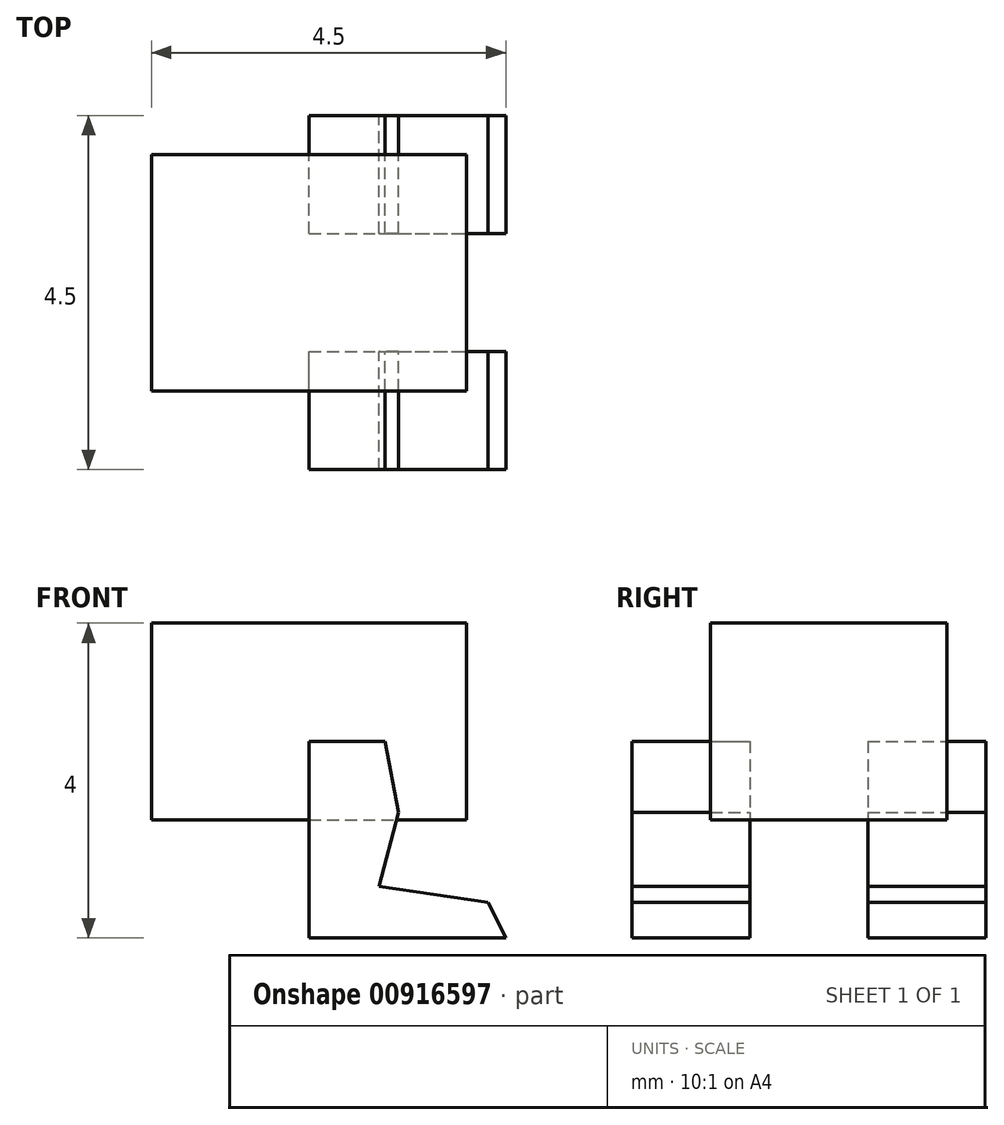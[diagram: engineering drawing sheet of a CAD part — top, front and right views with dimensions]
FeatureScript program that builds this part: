
annotation { "Feature Type Name" : "Feature", "Feature Type Description" : "" }
export const myFeature = defineFeature(function(context is Context, id is Id, definition is map)
    precondition{}
    {
        {
            var Q0;
            Q0=qCreatedBy(makeId("Front.planeOp"),FACE);
            var sketch = newSketch(context, id + "F0", { "sketchPlane" : qUnion([Q0])});
            skLineSegment(sketch, "E0.bottom", {"start": v(0, 0) * mm, "end": v(4, 0) * mm});
            skLineSegment(sketch, "E0.top", {"start": v(0, 2.5) * mm, "end": v(4, 2.5) * mm});
            skLineSegment(sketch, "E0.left", {"start": v(0, 0) * mm, "end": v(0, 2.5) * mm});
            skLineSegment(sketch, "E0.right", {"start": v(4, 0) * mm, "end": v(4, 2.5) * mm});
            skSolve(sketch);
        }
        {
            var Q0;
            Q0=makeQuery(id+"F0.imprint","IMPRINT",FACE,{"disambiguationData":[TD([[makeQuery(id+"F0.imprint","IMPRINT",EDGE,{"derivedFrom":sQuery(id+"F0.wireOp",EDGE,"E0.bottom")}),1.0]])]});
            extrude(context, id + "F1", {"entities" : qUnion([Q0]), "depth" : 3 * mm, "offsetDistance" : 25 * mm});
        }
        {
            var Q0;
            Q0=qCreatedBy(makeId("Front.planeOp"),FACE);
            var sketch = newSketch(context, id + "F2", { "sketchPlane" : qUnion([Q0])});
            skLineSegment(sketch, "E1.bottom", {"start": v(4.9, 1) * mm, "end": v(5.86, 1) * mm});
            skLineSegment(sketch, "E1.top", {"start": v(4.9, -1.5) * mm, "end": v(7.4, -1.5) * mm});
            skLineSegment(sketch, "E1.left", {"start": v(4.9, 1) * mm, "end": v(4.9, -1.5) * mm});
            skLineSegment(sketch, "E2", {"start": v(5.86, 1) * mm, "end": v(6.03, 0.09) * mm});
            skLineSegment(sketch, "E3", {"start": v(6.03, 0.09) * mm, "end": v(5.79, -0.85) * mm});
            skLineSegment(sketch, "E4", {"start": v(5.79, -0.85) * mm, "end": v(7.17, -1.05) * mm});
            skLineSegment(sketch, "E5", {"start": v(7.17, -1.05) * mm, "end": v(7.4, -1.5) * mm});
            skSolve(sketch);
        }
        {
            var Q0;
            Q0=makeQuery(id+"F2.imprint","IMPRINT",FACE,{"disambiguationData":[TD([[makeQuery(id+"F2.imprint","IMPRINT",EDGE,{"derivedFrom":sQuery(id+"F2.wireOp",EDGE,"E1.bottom")}),-1.0]])]});
            extrude(context, id + "F3", {"entities" : qUnion([Q0]), "depth" : 1.5 * mm, "offsetDistance" : 25 * mm});
        }
        {
            var Q0;
            Q0=makeQuery(id+"F1.opExtrude","CAP_EDGE",EDGE,{"disambiguationData":[OSD([sQuery(id+"F0.wireOp",EDGE,"E0.bottom")])],"isStart":false});
            cPoint(context, id + "F4", {"entities" : qUnion([Q0]), "parameter" : 0.5});
        }
        {
            var Q0;
            Q0=makeQuery(id+"F3.opExtrude","SWEPT_BODY",BODY,{"disambiguationData":[OSD([sQuery(id+"F2.wireOp",EDGE,"E1.bottom"),sQuery(id+"F2.wireOp",EDGE,"E1.top"),sQuery(id+"F2.wireOp",EDGE,"E1.left"),sQuery(id+"F2.wireOp",EDGE,"E2"),sQuery(id+"F2.wireOp",EDGE,"E3"),sQuery(id+"F2.wireOp",EDGE,"E4"),sQuery(id+"F2.wireOp",EDGE,"E5")])]});
            var Q1;
            Q1=makeQuery(id+"F3.opExtrude","CAP_VERTEX",VERTEX,{"disambiguationData":[OSD([sQuery(id+"F2.wireOp",EDGE,"E1.bottom"),sQuery(id+"F2.wireOp",EDGE,"E1.left")])],"isStart":true});
            var Q2;
            Q2 = qCreatedBy(id + "F4" ,VERTEX);
            transform(context, id + "F5", {"entities" : qUnion([Q0]), "transformType" : TransformType.TRANSLATION_ENTITY, "oppositeDirectionEntity" : false, "transformLine" : qUnion([Q1, Q2]), "makeCopy" : false});
        }
        {
            var Q0;
            Q0=makeQuery(id+"F1.opExtrude","CAP_EDGE",EDGE,{"disambiguationData":[OSD([sQuery(id+"F0.wireOp",EDGE,"E0.bottom")])],"isStart":false});
            cPoint(context, id + "F6", {"entities" : qUnion([Q0]), "parameter" : 0.5});
        }
        {
            var Q0;
            Q0=makeQuery(id+"F3.opExtrude","SWEPT_BODY",BODY,{"disambiguationData":[OSD([sQuery(id+"F2.wireOp",EDGE,"E1.bottom"),sQuery(id+"F2.wireOp",EDGE,"E1.top"),sQuery(id+"F2.wireOp",EDGE,"E1.left"),sQuery(id+"F2.wireOp",EDGE,"E2"),sQuery(id+"F2.wireOp",EDGE,"E3"),sQuery(id+"F2.wireOp",EDGE,"E4"),sQuery(id+"F2.wireOp",EDGE,"E5")])]});
            var Q1;
            Q1 = qCreatedBy(id + "F6" ,VERTEX);
            var Q2;
            Q2=makeQuery(id+"F1.opExtrude","SWEPT_FACE",FACE,{"disambiguationData":[OSD([sQuery(id+"F0.wireOp",EDGE,"E0.top")])]});
            transform(context, id + "F7", {"entities" : qUnion([Q0]), "transformType" : TransformType.TRANSLATION_DISTANCE, "transformDirection" : qUnion([Q2]), "distance" : 1 * mm, "makeCopy" : false});
        }
        {
            var Q0;
            Q0=makeQuery(id+"F3.opExtrude","SWEPT_BODY",BODY,{"disambiguationData":[OSD([sQuery(id+"F2.wireOp",EDGE,"E1.bottom"),sQuery(id+"F2.wireOp",EDGE,"E1.top"),sQuery(id+"F2.wireOp",EDGE,"E1.left"),sQuery(id+"F2.wireOp",EDGE,"E2"),sQuery(id+"F2.wireOp",EDGE,"E3"),sQuery(id+"F2.wireOp",EDGE,"E4"),sQuery(id+"F2.wireOp",EDGE,"E5")])]});
            var Q1;
            Q1=qCreatedBy(makeId("Right.planeOp"),FACE);
            var Q2;
            Q2=qCreatedBy(makeId("Front.planeOp"),FACE);
            transform(context, id + "F8", {"entities" : qUnion([Q0]), "transformType" : TransformType.TRANSLATION_DISTANCE, "transformDirection" : qUnion([Q1, Q2]), "distance" : 3 * mm, "makeCopy" : true});
        }
        {
            var Q0;
            Q0=makeQuery(id+"F8.opPattern","COPY",BODY,{"derivedFrom":makeQuery(id+"F3.opExtrude","SWEPT_BODY",BODY,{"disambiguationData":[OSD([sQuery(id+"F2.wireOp",EDGE,"E1.bottom"),sQuery(id+"F2.wireOp",EDGE,"E1.top"),sQuery(id+"F2.wireOp",EDGE,"E1.left"),sQuery(id+"F2.wireOp",EDGE,"E2"),sQuery(id+"F2.wireOp",EDGE,"E3"),sQuery(id+"F2.wireOp",EDGE,"E4"),sQuery(id+"F2.wireOp",EDGE,"E5")])]}),"instanceName":"1"});
            deleteBodies(context, id + "F9", {"entities" : qUnion([Q0])});
        }
        {
            var Q0;
            Q0=makeQuery(id+"F3.opExtrude","SWEPT_BODY",BODY,{"disambiguationData":[OSD([sQuery(id+"F2.wireOp",EDGE,"E1.bottom"),sQuery(id+"F2.wireOp",EDGE,"E1.top"),sQuery(id+"F2.wireOp",EDGE,"E1.left"),sQuery(id+"F2.wireOp",EDGE,"E2"),sQuery(id+"F2.wireOp",EDGE,"E3"),sQuery(id+"F2.wireOp",EDGE,"E4"),sQuery(id+"F2.wireOp",EDGE,"E5")])]});
            var Q1;
            Q1=makeQuery(id+"F1.opExtrude","CAP_FACE",FACE,{"disambiguationData":[OSD([sQuery(id+"F0.wireOp",EDGE,"E0.bottom"),sQuery(id+"F0.wireOp",EDGE,"E0.top"),sQuery(id+"F0.wireOp",EDGE,"E0.left"),sQuery(id+"F0.wireOp",EDGE,"E0.right")])],"isStart":true});
            transform(context, id + "F10", {"entities" : qUnion([Q0]), "transformType" : TransformType.TRANSLATION_DISTANCE, "transformDirection" : qUnion([Q1]), "distance" : 3.5 * mm, "makeCopy" : true});
        }
        {
            var Q0;
            Q0=makeQuery(id+"F3.opExtrude","SWEPT_BODY",BODY,{"disambiguationData":[OSD([sQuery(id+"F2.wireOp",EDGE,"E1.bottom"),sQuery(id+"F2.wireOp",EDGE,"E1.top"),sQuery(id+"F2.wireOp",EDGE,"E1.left"),sQuery(id+"F2.wireOp",EDGE,"E2"),sQuery(id+"F2.wireOp",EDGE,"E3"),sQuery(id+"F2.wireOp",EDGE,"E4"),sQuery(id+"F2.wireOp",EDGE,"E5")])]});
            var Q1;
            Q1=makeQuery(id+"F1.opExtrude","CAP_FACE",FACE,{"disambiguationData":[OSD([sQuery(id+"F0.wireOp",EDGE,"E0.bottom"),sQuery(id+"F0.wireOp",EDGE,"E0.top"),sQuery(id+"F0.wireOp",EDGE,"E0.left"),sQuery(id+"F0.wireOp",EDGE,"E0.right")])],"isStart":true});
            transform(context, id + "F11", {"entities" : qUnion([Q0]), "transformType" : TransformType.TRANSLATION_DISTANCE, "transformDirection" : qUnion([Q1]), "distance" : .5 * mm, "makeCopy" : false});
        }
    });
